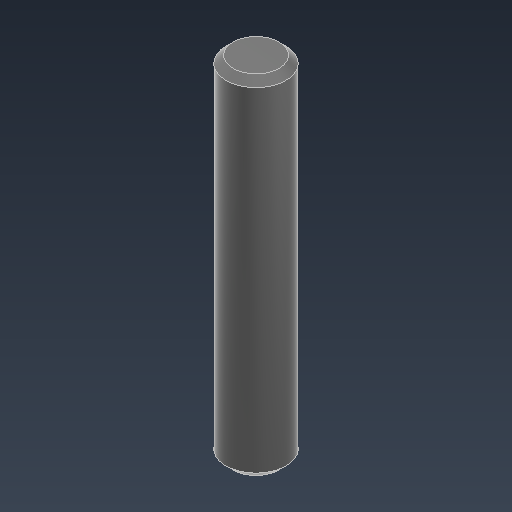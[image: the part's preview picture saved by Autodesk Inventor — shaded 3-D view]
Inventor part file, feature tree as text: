
AUTODESK INVENTOR PART (.ipt)
format: ipt  version: 2021.3 (Build 253353000, 353)  size: 94,208 bytes
history: native  units: mm
features: extrude x1, chamfer x1, sketch x1
ambient origin geometry x8: Origin, YZ Plane, XZ Plane, XY Plane, X Axis, Y Axis, Z Axis, Center Point
bodies: Solid1 (feature_tree)
feature tree (3):
  extrude  "Extrusion1"  Depth=25.0mm TaperAngle=0.0deg
  chamfer  "Chamfer1"  Distance=0.5mm Angle=45.0deg
  sketch  "Sketch1"  dims[d0=4.3mm d1=25.0mm d2=0.0mm d3=0.5mm d4=2.0mm d5=45.0deg]
